# Revit family: Plumbing Fixture-Grease_Interseptor_Mifab_MI-O
name_source: partatom
category: Plumbing Fixtures
revit_build: Autodesk Revit Structure 2013 (Build: 20120221_2030(x64)
units: mm (PartAtom-declared; Revit-internal decimal feet)

## types (17) — shared parameters
Assembly Code = D2090300
Description = 10 to 500 GPM Oil Interceptor
Interceptor Material = Acid Resistant Epoxy Coated Green
Manufacturer = MIFAB
URL = www.mifab.com
zero-valued in all types: Default Elevation, WFU

## per-type parameters (varying)
| type | A | B | C | D | E | F | Flow Rate | G | Model | Standard Inlet And Outlet Radii | Water Capacity |
| MI-0-A | 21.25 " | 15.75 " | 3.5 " | 9.5 " | 13 " | 2 " | 10 GPM | 4 " | MI-0-A | 1 " | 9.73 Gallons |
| MI-0-B | 23.75 " | 15.75 " | 3.5 " | 11.5 " | 15 " | 2 " | 15 GPM | 6 " | MI-0-B | 1 " | 13.59 Gallons |
| MI-0-C | 23.75 " | 15.75 " | 3.5 " | 14 " | 17.5 " | 3 " | 20 GPM | 8 " | MI-0-C | 1.5 " | 20.07 Gallons |
| MI-0-1 | 28 " | 22 " | 6 " | 26 " | 32 " | 3 " | 25 GPM | 19 " | MI-0-1 | 1.5 " | 55.15 Gallons |
| MI-0-2 | 34 " | 24 " | 6 " | 26 " | 32 " | 3 " | 35 GPM | 19 " | MI-0-2 | 1.5 " | 74.67 Gallons |
| MI-0-3 | 34 " | 24 " | 6 " | 28 " | 34 " | 3 " | 50 GPM | 21 " | MI-0-3 | 1.5 " | 80.76 Gallons |
| MI-0-4 | 48 " | 34 " | 8 " | 28 " | 36 " | 4 " | 75 GPM | 21 " | MI-0-4 | 2 " | 165.68 Gallons |
| MI-0-5 | 51 " | 36 " | 8 " | 28 " | 36 " | 4 " | 100 GPM | 21 " | MI-0-5 | 2 " | 245.21 Gallons |
| MI-0-6 | 53 " | 36 " | 8 " | 28 " | 36 " | 4 " | 125 GPM | 21 " | MI-0-6 | 2 " | 195.17 Gallons |
| MI-0-7 | 58 " | 36 " | 10 " | 28 " | 38 " | 4 " | 150 GPM | 21 " | MI-0-7 | 2 " | 214.30 Gallons |
| MI-0-8 | 68 " | 38 " | 10 " | 32 " | 42 " | 4 " | 200 GPM | 25 " | MI-0-8 | 2 " | 308.57 Gallons |
| MI-0-9 | 74 " | 40 " | 12 " | 38 " | 50 " | 4 " | 250 GPM | 31 " | MI-0-8 | 2 " | 426.39 Gallons |
| MI-0-10 | 78 " | 44 " | 12 " | 40 " | 52 " | 4 " | 300 GPM | 33 " | MI-0-10 | 2 " | 549.71 Gallons |
| MI-0-11 | 80 " | 46 " | 12 " | 40 " | 52 " | 6 " | 350 GPM | 33 " | MI-0-11 | 3 " | 621.30 Gallons |
| MI-0-12 | 82 " | 48 " | 12 " | 42 " | 54 " | 6 " | 400 GPM | 35 " | MI-0-12 | 3 " | 664.52 Gallons |
| MI-0-13 | 84 " | 50 " | 12 " | 42 " | 54 " | 6 " | 450 GPM | 35 " | MI-0-13 | 3 " | 690.91 Gallons |
| MI-0-14 | 86 " | 52 " | 12 " | 46 " | 58 " | 6 " | 500 GPM | 39 " | MI-0-14 | 3 " | 781.82 Gallons |

## geometry (parser evidence)
native form markers: Blend x5, Sweep x1
no freeform markers — native parametric forms only
